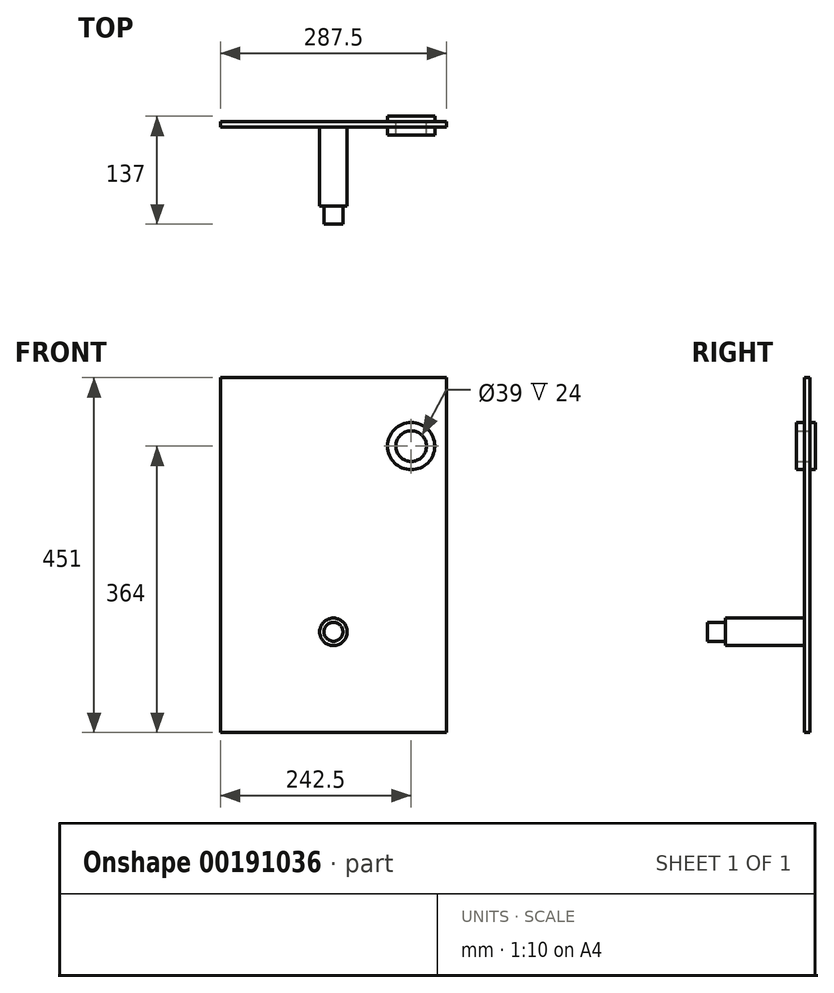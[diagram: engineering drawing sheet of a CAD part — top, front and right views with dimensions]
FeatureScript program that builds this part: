
annotation { "Feature Type Name" : "Feature", "Feature Type Description" : "" }
export const myFeature = defineFeature(function(context is Context, id is Id, definition is map)
    precondition{}
    {
        {
            var Q0;
            Q0=qCreatedBy(makeId("Front.planeOp"),FACE);
            var sketch = newSketch(context, id + "F0", { "sketchPlane" : qUnion([Q0])});
            skLineSegment(sketch, "E0.bottom", {"start": v(143.75, 225.5) * mm, "end": v(-143.75, 225.5) * mm});
            skLineSegment(sketch, "E0.top", {"start": v(143.75, -225.5) * mm, "end": v(-143.75, -225.5) * mm});
            skLineSegment(sketch, "E0.left", {"start": v(143.75, 225.5) * mm, "end": v(143.75, -225.5) * mm});
            skLineSegment(sketch, "E0.right", {"start": v(-143.75, 225.5) * mm, "end": v(-143.75, -225.5) * mm});
            skPoint(sketch, "E0.middle", {"position": v(0, 0) * mm});
            skSolve(sketch);
        }
        {
            var Q0;
            Q0 = qSketchRegion(id + "F0", true);
            extrude(context, id + "F1", {"entities" : qUnion([Q0]), "depth" : 7 * mm});
        }
        {
            var Q0;
            Q0=makeQuery(id+"F1.opExtrude","CAP_FACE",FACE,{"disambiguationData":[OSD([sQuery(id+"F0.wireOp",EDGE,"E0.bottom"),sQuery(id+"F0.wireOp",EDGE,"E0.top"),sQuery(id+"F0.wireOp",EDGE,"E0.left"),sQuery(id+"F0.wireOp",EDGE,"E0.right")])],"isStart":false});
            var sketch = newSketch(context, id + "F2", { "sketchPlane" : qUnion([Q0])});
            skCircle(sketch, "E1", {"center": v(0, -97.5) * mm, "radius": 17.5 * mm});
            skCircle(sketch, "E2", {"center": v(98.75, 138.5) * mm, "radius": 19.5 * mm});
            skCircle(sketch, "E3", {"center": v(98.75, 138.5) * mm, "radius": 30 * mm});
            skSolve(sketch);
        }
        {
            var Q0;
            Q0=makeQuery(id+"F2.imprint","IMPRINT",FACE,{"disambiguationData":[TD([[makeQuery(id+"F2.imprint","IMPRINT",EDGE,{"derivedFrom":sQuery(id+"F2.wireOp",EDGE,"E2")}),-1.0]])]});
            extrude(context, id + "F3", {"entities" : qUnion([Q0]), "operationType" : NewBodyOperationType.ADD, "depth" : 10 * mm});
        }
        {
            var Q0;
            Q0=makeQuery(id+"F3.boolean.opBoolean","SPLIT",FACE,{"disambiguationData":[TD([makeQuery(id+"F3.opExtrude","SWEPT_FACE",FACE,{"disambiguationData":[OSD([sQuery(id+"F2.wireOp",EDGE,"E2")])]})])],"derivedFrom":makeQuery(id+"F1.opExtrude","CAP_FACE",FACE,{"disambiguationData":[OSD([sQuery(id+"F0.wireOp",EDGE,"E0.bottom"),sQuery(id+"F0.wireOp",EDGE,"E0.top"),sQuery(id+"F0.wireOp",EDGE,"E0.left"),sQuery(id+"F0.wireOp",EDGE,"E0.right")])],"isStart":false})});
            extrude(context, id + "F4", {"entities" : qUnion([Q0]), "operationType" : NewBodyOperationType.REMOVE, "oppositeDirection" : true, "depth" : 25 * mm});
        }
        {
            var Q0;
            Q0=makeQuery(id+"F3.opExtrude","CAP_FACE",FACE,{"disambiguationData":[OSD([sQuery(id+"F2.wireOp",EDGE,"E2"),sQuery(id+"F2.wireOp",EDGE,"E3")])],"isStart":false});
            extrude(context, id + "F5", {"entities" : qUnion([Q0]), "operationType" : NewBodyOperationType.ADD, "oppositeDirection" : true, "depth" : 24 * mm});
        }
        {
            var Q0;
            Q0=makeQuery(id+"F2.imprint","IMPRINT",FACE,{"disambiguationData":[TD([[makeQuery(id+"F2.imprint","IMPRINT",EDGE,{"derivedFrom":sQuery(id+"F2.wireOp",EDGE,"E1")}),1.0]])]});
            extrude(context, id + "F6", {"entities" : qUnion([Q0]), "operationType" : NewBodyOperationType.ADD, "depth" : 100 * mm});
        }
        {
            var Q0;
            Q0=makeQuery(id+"F6.opExtrude","CAP_FACE",FACE,{"disambiguationData":[OSD([sQuery(id+"F2.wireOp",EDGE,"E1")])],"isStart":false});
            var sketch = newSketch(context, id + "F7", { "sketchPlane" : qUnion([Q0])});
            skCircle(sketch, "E4", {"center": v(0, -97.5) * mm, "radius": 12 * mm});
            skSolve(sketch);
        }
        {
            var Q0;
            Q0 = qSketchRegion(id + "F7", true);
            extrude(context, id + "F8", {"entities" : qUnion([Q0]), "operationType" : NewBodyOperationType.ADD, "depth" : 23 * mm});
        }
    });
